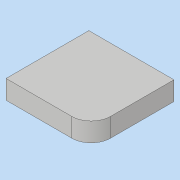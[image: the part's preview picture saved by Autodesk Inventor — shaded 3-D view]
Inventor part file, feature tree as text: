
AUTODESK INVENTOR PART (.ipt)
format: ipt  version: 2019 (Build 230136000, 136)  size: 89,088 bytes
history: native  units: mm
features: sketch x3, extrude x1, fillet x1
ambient origin geometry x8: Origin, YZ Plane, XZ Plane, XY Plane, X Axis, Y Axis, Z Axis, Center Point
bodies: Body1 (feature_tree)
feature tree (5):
  extrude  "Выдавливание2"  TaperAngle=0.0deg  [1 undecoded]
  fillet  "Сопряжение1"  Radius=42.0mm
  sketch  "Эскиз1"
  sketch  "Эскиз2"
  sketch  "Эскиз3"
note: 1 required parameter value undecoded (feature->parameter linkage not recoverable at this tier; creation-order binding heuristic only, values carry confidence <= 0.55)
